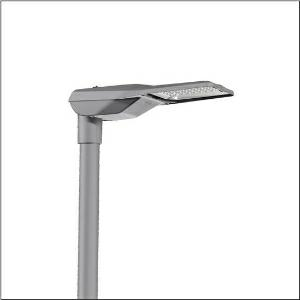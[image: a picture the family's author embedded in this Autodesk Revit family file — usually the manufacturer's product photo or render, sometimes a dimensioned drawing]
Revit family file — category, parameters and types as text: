
# Revit family: streetlight_sl_21_mini___st0_5a_5xe2b33s08hb_7adc
name_source: partatom
category: Lighting Fixtures
units: mm (PartAtom-declared; Revit-internal decimal feet)

## family parameters
Cut with Voids When Loaded = No
Host = Face
Light Source = No
Part Type = Normal
Room Calculation Point = No
Round Connector Dimension = Use Diameter
Shared = No

## types (1)
- --- (1 x LED, 9040 lm, 66 W, 3000K)
    Apparent Load = 66 VA
    CIE Flux Codes = 41 75 97 100 100
    Color Rendering = 70
    Color Temperature = 3000K
    Default Elevation = 1800 mm
    Description = Streetlight SL 21 mini, mast luminaire, primary light control with lens, of PMMA, primary optical cover: cover, of toughened safety glass, transparent, light distribution: ST0.5a, light emission: direct distribution, primary light characteristic: asymmetric, installation type: side-entry, post-top, LED, High Power LED, rated luminous flux: 9.040lm, luminous efficacy: 137lm/W, light colour: 730, colour temperature: 3000K, control gear: D4i, control: overheat protection, constant luminous flux control, time-dependent luminous flux control, flexible luminous flux parameterisation, pre-setting: logarithmic dimming characteristic, mains connection: 220..240V, AC, 50/60Hz, start of lifetime: 66W, end of service life: 69W, reduction: 30W, luminaire housing, of diecast aluminium, powder-coated, Siteco® metallic grey (DB 702S), corrosivity category C5 mid according to DIN EN ISO 12944, please order mast flange separately, inclination adjustable: 0°, 5°, 10°, 15°, sealing non-destructively replaceable, multi-level sealing system, length: 628mm, width: 235mm, height: 110mm, mast flange for spigot size: 42mm (side-entry): 5XC10008XM4, 60/48mm (side-entry/post-top): 5XC10108XM2, 76/60mm (side-entry/post-top): 5XC10108XM1, mounting height: 4..8m, Smart Interface above, protection rating (complete): IP66, insulation class (complete): insulation class II (safety insulation), certification: CE, ENEC, ENEC+, VDE, impact resistance: IK10, permissible operating ambient temperature for outdoor applications: -40..+50°C, standard-compliant lighting for roads and squares, packaging unit: 1 piece

Light Distribution: ST0.5a
    Height = 110 mm
    Lamp = 1 x LED
    Lamp Light Flux = 9040 lm
    Lamp Power = 66 W
    Lamp count = 1
    Length = 625 mm
    Luminous efficacy = 137 lm/W
    Manufacturer = Siteco
    ModVariant = No
    Model = 5XE2B33S08HB
    Number of Poles = 1
    OnlyDefault = Yes
    Power Factor = 1
    Product Name = Streetlight SL 21 mini | ST0.5a
    Product group = mast luminaire | pylon top
    ProductGroupID = 6100
    Protection Class = Protection class II
    Protection Degree = IP 66
    RLX_Detail_Level = 1
    RLX_Emergency_Light_Flux = 0 lm
    RLX_Emergency_Type = 0
    RLX_Emergency_Type_DB = No
    RlxData = <blob elided: 37157 chars, md5=71a615b0>
    Socket = socket
    Standby Power = 0 W
    System Light Flux = 9040 lm
    System Power = 66 W
    Type Comments = factory setting: luminous flux: 100 % | dim-lin: 254 | 670 mA
    Type Image = l_1003515.jpg
    URL = http://relux.com
    VarID = @adj_212487
    Voltage = 0 V
    Weight = 0.00 kg
    Width = 234 mm

## geometry (parser evidence)
native form markers: Blend x4, Sweep x12
no freeform markers — native parametric forms only
